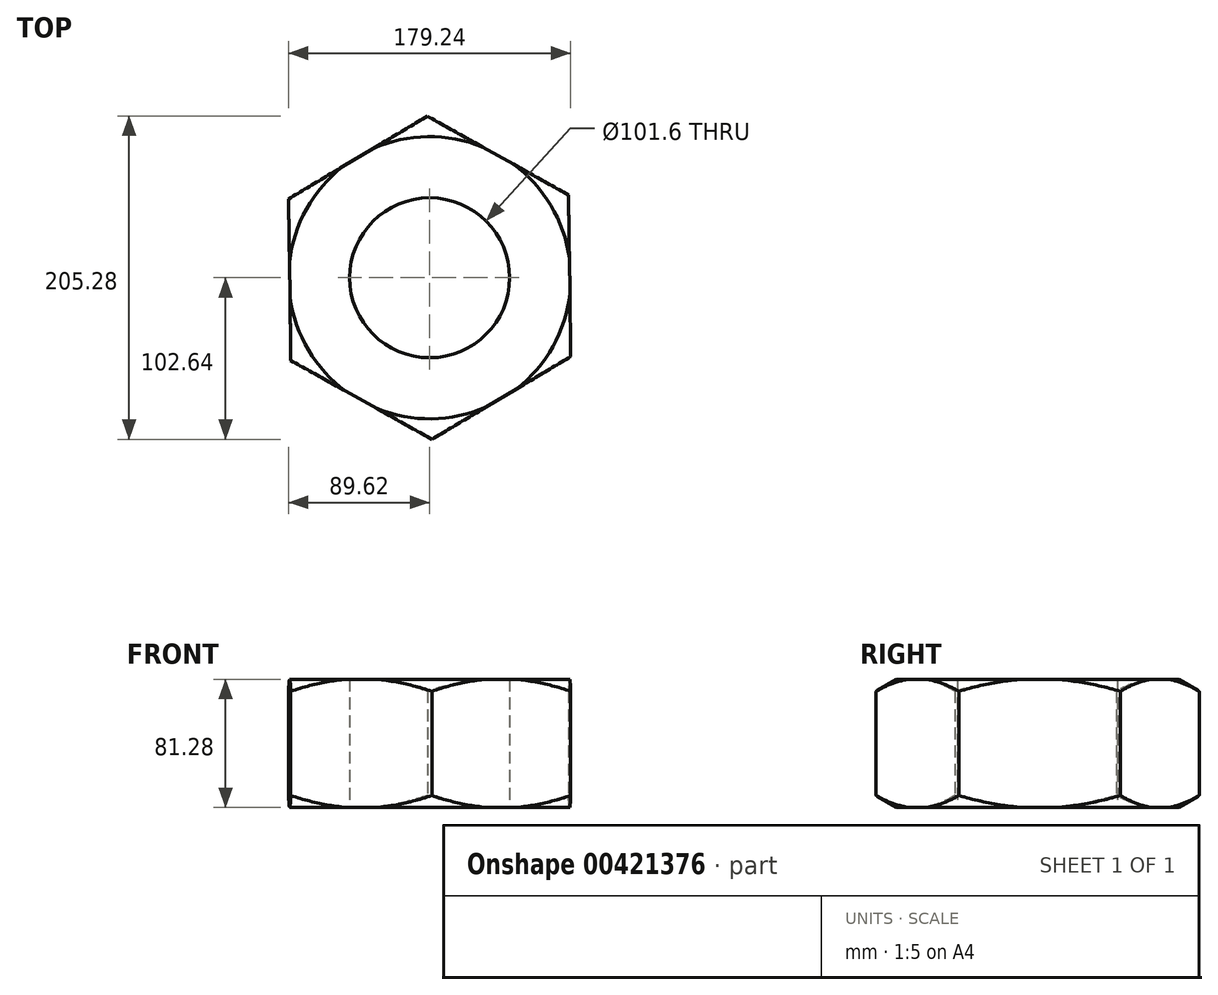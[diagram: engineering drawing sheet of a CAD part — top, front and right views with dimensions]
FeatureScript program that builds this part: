
annotation { "Feature Type Name" : "Feature", "Feature Type Description" : "" }
export const myFeature = defineFeature(function(context is Context, id is Id, definition is map)
    precondition{}
    {
        {
            var Q0;
            Q0=qCreatedBy(makeId("Top.planeOp"),FACE);
            var sketch = newSketch(context, id + "F0", { "sketchPlane" : qUnion([Q0])});
            skCircle(sketch, "E0.cCircle", {"center": v(0, 0) * mm, "radius": 88.9 * mm, "construction": true});
            skLineSegment(sketch, "E0.0", {"start": v(-1.46, 102.64) * mm, "end": v(88.16, 52.58) * mm});
            skLineSegment(sketch, "E0.1", {"start": v(88.16, 52.58) * mm, "end": v(89.62, -50.06) * mm});
            skLineSegment(sketch, "E0.2", {"start": v(89.62, -50.06) * mm, "end": v(1.46, -102.64) * mm});
            skLineSegment(sketch, "E0.3", {"start": v(1.46, -102.64) * mm, "end": v(-88.16, -52.58) * mm});
            skLineSegment(sketch, "E0.4", {"start": v(-88.16, -52.58) * mm, "end": v(-89.62, 50.06) * mm});
            skLineSegment(sketch, "E0.5", {"start": v(-89.62, 50.06) * mm, "end": v(-1.46, 102.64) * mm});
            skPoint(sketch, "E0.0.midPoint", {"position": v(43.35, 77.61) * mm});
            skCircle(sketch, "E1", {"center": v(0, 0) * mm, "radius": 50.8 * mm});
            skSolve(sketch);
        }
        {
            var Q0;
            Q0 = qSketchRegion(id + "F0", true);
            extrude(context, id + "F1", {"entities" : qUnion([Q0]), "depth" : 81.28 * mm});
        }
        {
            var Q0;
            Q0=qCreatedBy(makeId("Front.planeOp"),FACE);
            var sketch = newSketch(context, id + "F2", { "sketchPlane" : qUnion([Q0])});
            skLineSegment(sketch, "E2", {"start": v(0, 0) * mm, "end": v(0, 81.28) * mm, "construction": true});
            skLineSegment(sketch, "E3", {"start": v(0, 40.64) * mm, "end": v(89.62, 40.64) * mm, "construction": true});
            skPoint(sketch, "E3.endSnap0", {"position": v(0, 40.64) * mm});
            skLineSegment(sketch, "E4", {"start": v(157.83, 81.28) * mm, "end": v(89.62, 81.28) * mm});
            skLineSegment(sketch, "E5", {"start": v(89.62, 81.28) * mm, "end": v(161.25, 39.93) * mm});
            skLineSegment(sketch, "E6", {"start": v(161.25, 39.93) * mm, "end": v(157.83, 81.28) * mm});
            skLineSegment(sketch, "E7.MirrorCS", {"start": v(89.62, 0) * mm, "end": v(161.25, 41.35) * mm});
            skLineSegment(sketch, "E8.MirrorCS", {"start": v(157.83, 0) * mm, "end": v(89.62, 0) * mm});
            skLineSegment(sketch, "E9.MirrorCS", {"start": v(161.25, 41.35) * mm, "end": v(157.83, 0) * mm});
            skSolve(sketch);
        }
        {
            var Q0;
            Q0 = qSketchRegion(id + "F2", true);
            var Q1;
            Q1=sQuery(id+"F2.wireOp",EDGE,"E2");
            revolve(context, id + "F3", {"operationType" : NewBodyOperationType.REMOVE, "entities" : qUnion([Q0]), "axis" : qUnion([Q1]), "revolveType" : RevolveType.FULL});
        }
    });
